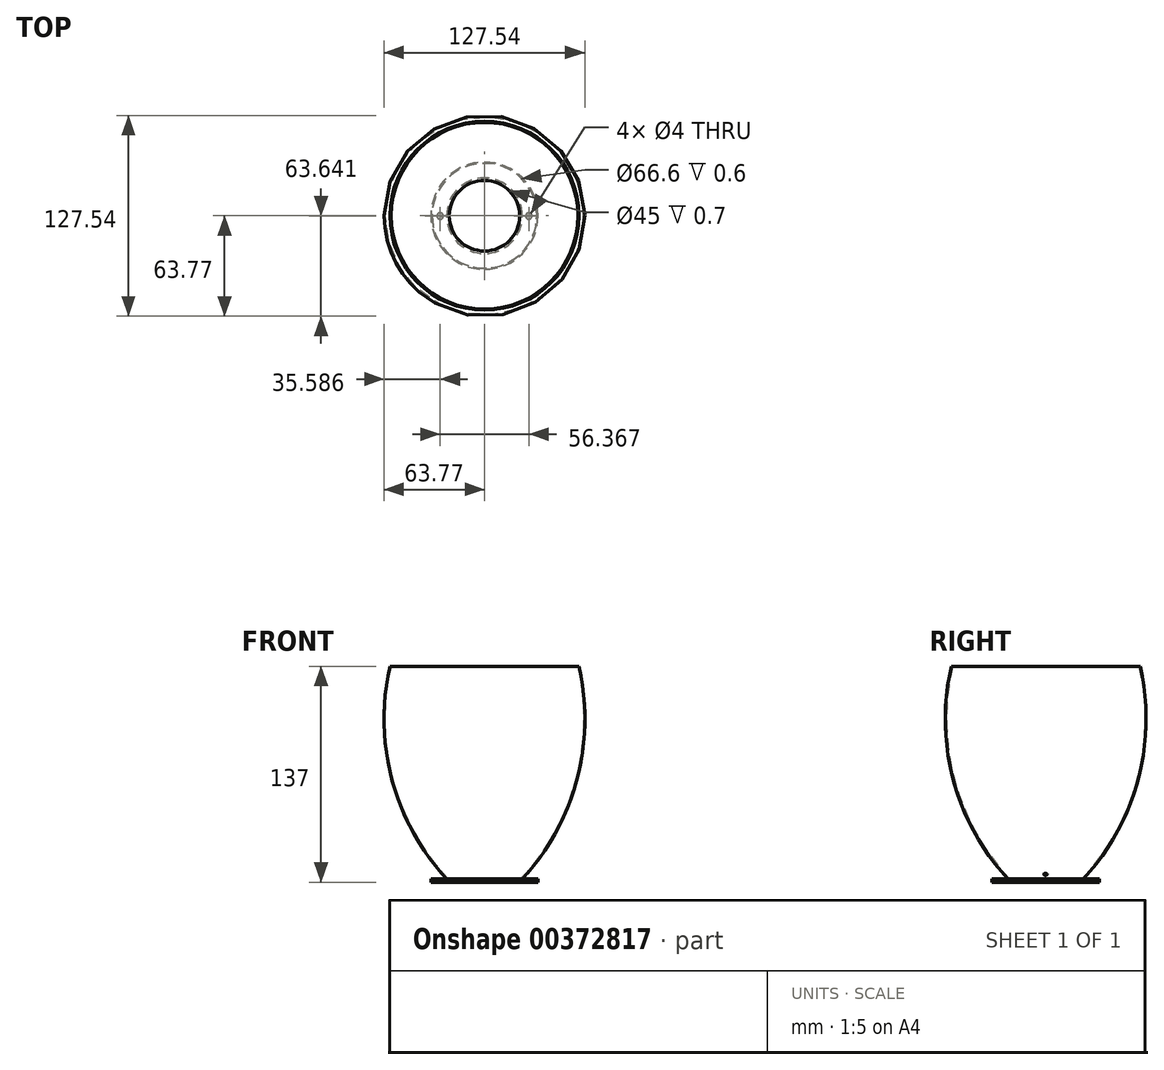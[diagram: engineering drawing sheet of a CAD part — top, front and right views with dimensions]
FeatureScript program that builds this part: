
annotation { "Feature Type Name" : "Feature", "Feature Type Description" : "" }
export const myFeature = defineFeature(function(context is Context, id is Id, definition is map)
    precondition{}
    {
        {
            var Q0;
            Q0=qCreatedBy(makeId("Front.planeOp"),FACE);
            var sketch = newSketch(context, id + "F0", { "sketchPlane" : qUnion([Q0])});
            skLineSegment(sketch, "E0", {"start": v(0, 0) * mm, "end": v(-24, 0) * mm});
            skLineSegment(sketch, "E1", {"start": v(0, 135) * mm, "end": v(-60, 135) * mm});
            skArc(sketch, "E2", {"start": v(-60, 135) * mm, "mid": v(-58.72, 63.04) * mm, "end": v(-24, 0) * mm});
            skLineSegment(sketch, "E3", {"start": v(0, 65) * mm, "end": v(0, -29.8) * mm, "construction": true});
            skLineSegment(sketch, "E4.MirrorCS", {"start": v(0, 135) * mm, "end": v(60, 135) * mm});
            skArc(sketch, "E5.MirrorCS", {"start": v(60, 135) * mm, "mid": v(58.72, 63.04) * mm, "end": v(24, 0) * mm});
            skLineSegment(sketch, "E6.MirrorCS", {"start": v(0, 0) * mm, "end": v(24, 0) * mm});
            skPoint(sketch, "E7", {"position": v(-24, 0) * mm});
            skPoint(sketch, "E8", {"position": v(-56, 54) * mm});
            skPoint(sketch, "E9", {"position": v(-11.75, -11.83) * mm});
            skPoint(sketch, "E10", {"position": v(-22.26, -1.85) * mm});
            skLineSegment(sketch, "E11", {"start": v(0, 0) * mm, "end": v(0, 195.4) * mm, "construction": true});
            skLineSegment(sketch, "E12", {"start": v(0, 0) * mm, "end": v(0, 135) * mm});
            skLineSegment(sketch, "E13", {"start": v(24, 0) * mm, "end": v(34, 0) * mm});
            skLineSegment(sketch, "E14", {"start": v(34, 0) * mm, "end": v(34, -2) * mm});
            skLineSegment(sketch, "E15", {"start": v(34, -2) * mm, "end": v(0, -2) * mm});
            skLineSegment(sketch, "E16", {"start": v(0, -2) * mm, "end": v(0, 0) * mm});
            skSolve(sketch);
        }
        {
            var Q0;
            Q0=makeQuery(id+"F0.imprint","IMPRINT",FACE,{"disambiguationData":[TD([[makeQuery(id+"F0.imprint","IMPRINT",EDGE,{"derivedFrom":sQuery(id+"F0.wireOp",EDGE,"E4.MirrorCS")}),-1.0]])]});
            var Q1;
            Q1=makeQuery(id+"F0.imprint","IMPRINT",FACE,{"disambiguationData":[TD([[makeQuery(id+"F0.imprint","IMPRINT",EDGE,{"derivedFrom":sQuery(id+"F0.wireOp",EDGE,"E6.MirrorCS")}),-1.0]])]});
            var Q2;
            Q2=sQuery(id+"F0.wireOp",EDGE,"E12");
            revolve(context, id + "F1", {"surfaceOperationType" : NewSurfaceOperationType.NEW, "entities" : qUnion([Q0, Q1]), "axis" : qUnion([Q2]), "revolveType" : RevolveType.FULL});
        }
        {
            var Q0;
            Q0=makeQuery(id+"F1.opRevolve","SWEPT_FACE",FACE,{"disambiguationData":[OSD([sQuery(id+"F0.wireOp",EDGE,"E4.MirrorCS")])]});
            var Q1;
            Q1=makeQuery(id+"F1.opRevolve","SWEPT_FACE",FACE,{"disambiguationData":[OSD([sQuery(id+"F0.wireOp",EDGE,"E6.MirrorCS")])]});
            shell(context, id + "F2", {"entities" : qUnion([Q0, Q1]), "thickness" : 0.7 * mm});
        }
        {
            var Q0;
            Q0=makeQuery(id+"F2.opShell","OFFSET_FACE",FACE,{"disambiguationData":[OSD([sQuery(id+"F0.wireOp",EDGE,"E15")])]});
            var sketch = newSketch(context, id + "F3", { "sketchPlane" : qUnion([Q0])});
            skCircle(sketch, "E17", {"center": v(0, 0) * mm, "radius": 22.5 * mm});
            skSolve(sketch);
        }
        {
            var Q0;
            Q0 = qSketchRegion(id + "F3", true);
            extrude(context, id + "F4", {"entities" : qUnion([Q0]), "operationType" : NewBodyOperationType.REMOVE, "endBound" : BoundingType.THROUGH_ALL, "oppositeDirection" : true, "depth" : 25 * mm, "offsetDistance" : 25 * mm});
        }
        {
            var Q0;
            Q0=makeQuery(id+"F1.opRevolve","SWEPT_FACE",FACE,{"disambiguationData":[OSD([sQuery(id+"F0.wireOp",EDGE,"E15")])]});
            var sketch = newSketch(context, id + "F5", { "sketchPlane" : qUnion([Q0])});
            skCircle(sketch, "E18", {"center": v(-28.18, 0.13) * mm, "radius": 2.3 * mm});
            skCircle(sketch, "E19.MirrorC", {"center": v(28.18, 0.13) * mm, "radius": 2.3 * mm});
            skSolve(sketch);
        }
        {
            var Q0;
            Q0=sQuery(id+"F5.wireOp",VERTEX,"E18.center");
            var Q1;
            Q1=sQuery(id+"F5.wireOp",VERTEX,"E19.MirrorC.center");
            var Q2;
            Q2=makeQuery(id+"F1.opRevolve","SWEPT_BODY",BODY,{"disambiguationData":[OSD([sQuery(id+"F0.wireOp",EDGE,"E4.MirrorCS"),sQuery(id+"F0.wireOp",EDGE,"E5.MirrorCS"),sQuery(id+"F0.wireOp",EDGE,"E12"),sQuery(id+"F0.wireOp",EDGE,"E13"),sQuery(id+"F0.wireOp",EDGE,"E14"),sQuery(id+"F0.wireOp",EDGE,"E15"),sQuery(id+"F0.wireOp",EDGE,"E16")])]});
            hole(context, id + "F6", {"style" : HoleStyle.SIMPLE, "endStyle" : HoleEndStyle.BLIND, "holeDiameter" : 4 * mm, "majorDiameter" : 5 * mm, "holeDepth" : 5 * mm, "isTappedThrough" : true, "tappedDepth" : 12 * mm, "tapClearance" : 3, "locations" : qUnion([Q0, Q1]), "scope" : qUnion([Q2])});
        }
    });
